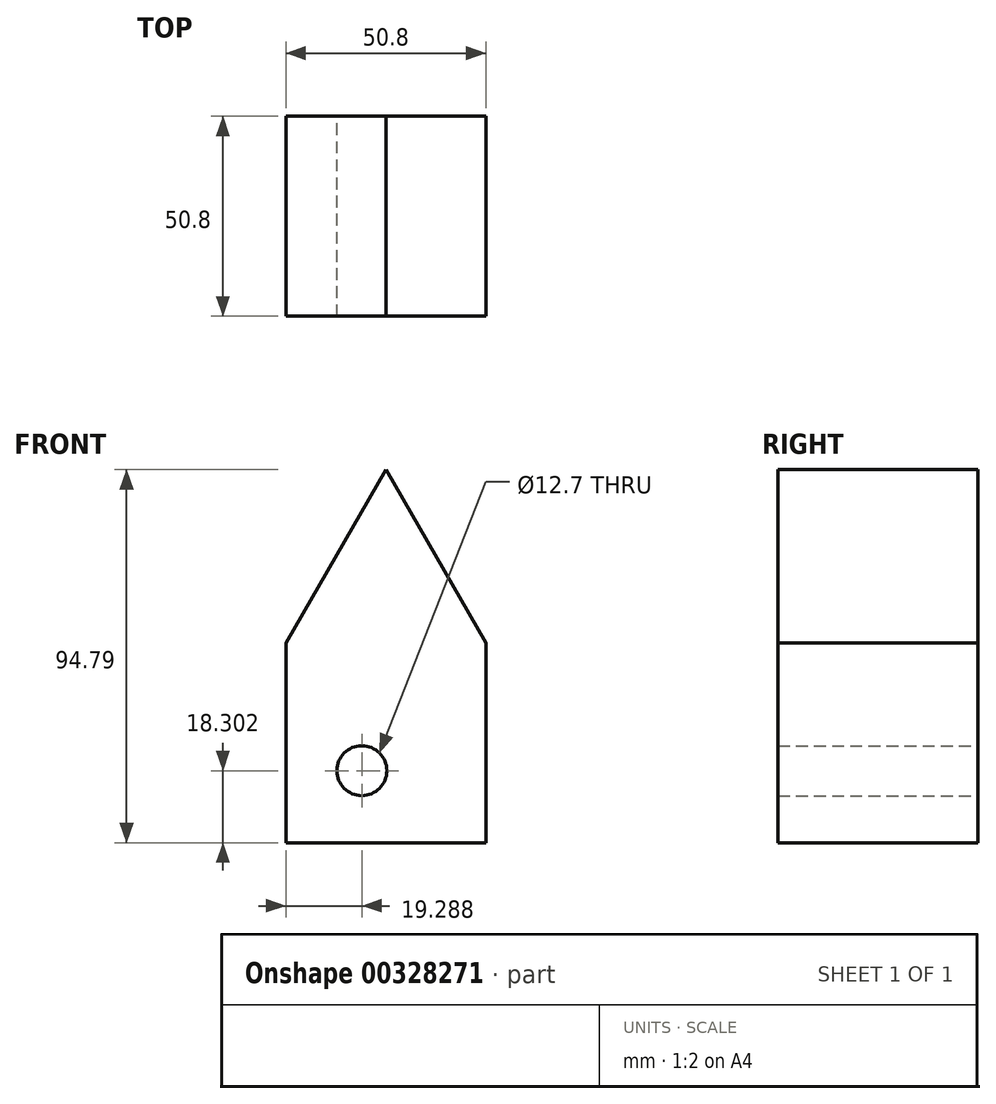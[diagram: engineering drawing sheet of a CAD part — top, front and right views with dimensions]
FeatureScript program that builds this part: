
annotation { "Feature Type Name" : "Feature", "Feature Type Description" : "" }
export const myFeature = defineFeature(function(context is Context, id is Id, definition is map)
    precondition{}
    {
        {
            var Q0;
            Q0=qCreatedBy(makeId("Front.planeOp"),FACE);
            var sketch = newSketch(context, id + "F0", { "sketchPlane" : qUnion([Q0])});
            skLineSegment(sketch, "E0.top", {"start": v(-25.4, -33.52) * mm, "end": v(25.4, -33.52) * mm});
            skLineSegment(sketch, "E0.left", {"start": v(-25.4, 17.28) * mm, "end": v(-25.4, -33.52) * mm});
            skLineSegment(sketch, "E0.right", {"start": v(25.4, 17.28) * mm, "end": v(25.4, -33.52) * mm});
            skLineSegment(sketch, "E1", {"start": v(25.4, 17.28) * mm, "end": v(0, 61.27) * mm});
            skLineSegment(sketch, "E2", {"start": v(-25.4, 17.28) * mm, "end": v(0, 61.27) * mm});
            skCircle(sketch, "E3", {"center": v(-6.11, -15.22) * mm, "radius": 6.35 * mm});
            skSolve(sketch);
        }
        {
            var Q0;
            Q0=makeQuery(id+"F0.imprint","IMPRINT",FACE,{"disambiguationData":[TD([[makeQuery(id+"F0.imprint","IMPRINT",EDGE,{"derivedFrom":sQuery(id+"F0.wireOp",EDGE,"E0.top")}),1.0]])]});
            extrude(context, id + "F1", {"entities" : qUnion([Q0]), "depth" : 50.8 * mm});
        }
    });
